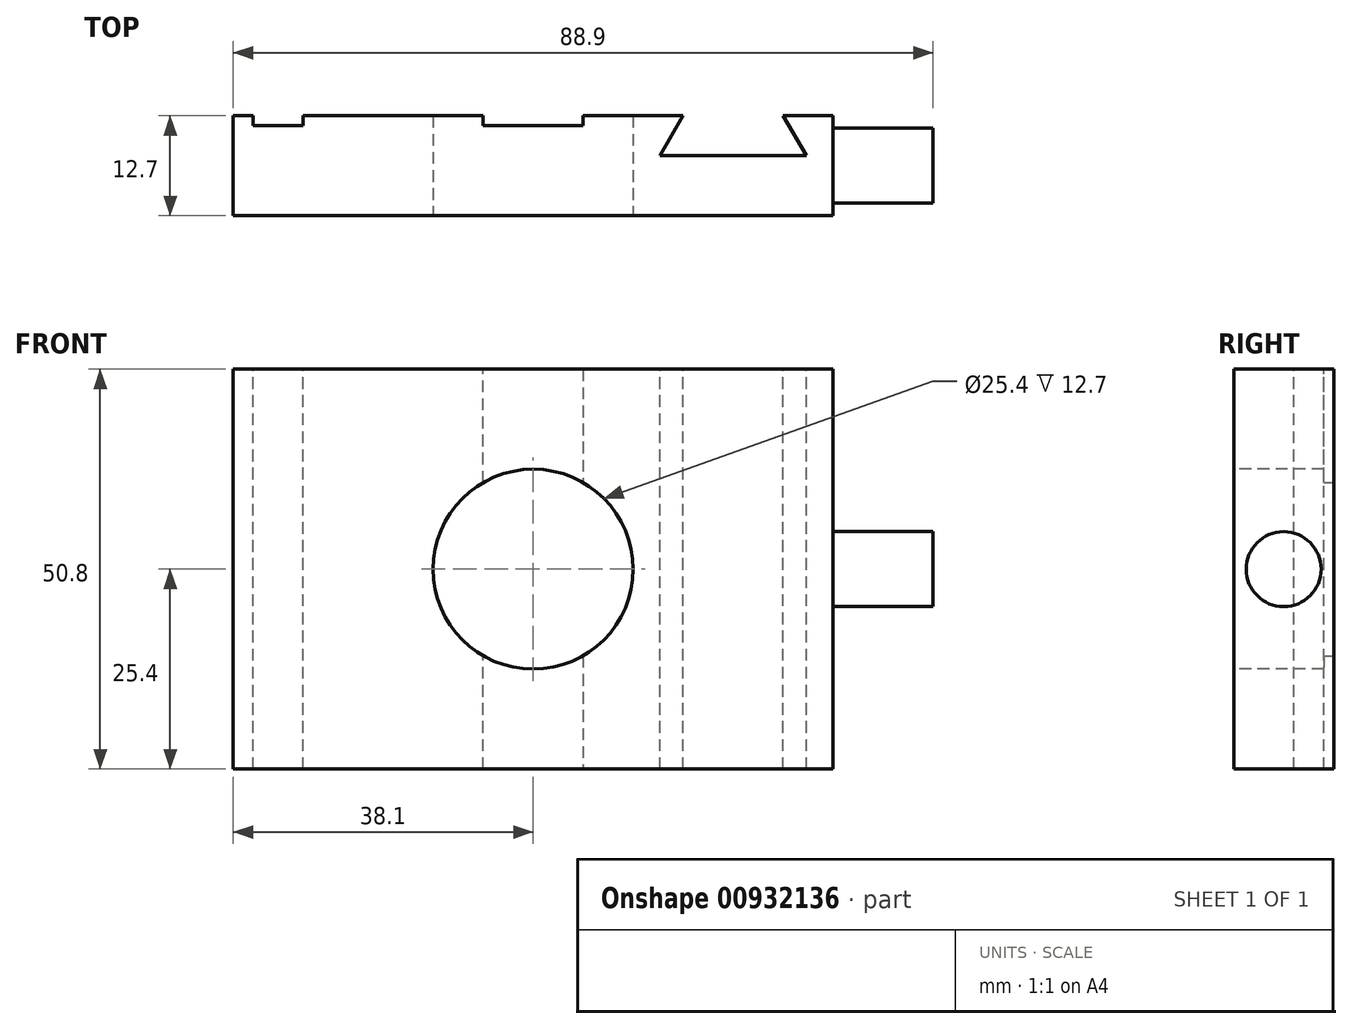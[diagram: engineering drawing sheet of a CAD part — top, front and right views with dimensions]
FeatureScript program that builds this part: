
annotation { "Feature Type Name" : "Feature", "Feature Type Description" : "" }
export const myFeature = defineFeature(function(context is Context, id is Id, definition is map)
    precondition{}
    {
        {
            var Q0;
            Q0=qCreatedBy(makeId("Front.planeOp"),FACE);
            var sketch = newSketch(context, id + "F0", { "sketchPlane" : qUnion([Q0])});
            skLineSegment(sketch, "E0.bottom", {"start": v(-38.1, 25.4) * mm, "end": v(38.1, 25.4) * mm});
            skLineSegment(sketch, "E0.top", {"start": v(-38.1, -25.4) * mm, "end": v(38.1, -25.4) * mm});
            skLineSegment(sketch, "E0.left", {"start": v(-38.1, 25.4) * mm, "end": v(-38.1, -25.4) * mm});
            skLineSegment(sketch, "E0.right", {"start": v(38.1, 25.4) * mm, "end": v(38.1, -25.4) * mm});
            skPoint(sketch, "E0.middle", {"position": v(0, 0) * mm});
            skCircle(sketch, "E1", {"center": v(0, 0) * mm, "radius": 12.7 * mm});
            skSolve(sketch);
        }
        {
            var Q0;
            Q0=makeQuery(id+"F0.imprint","IMPRINT",FACE,{"disambiguationData":[TD([[makeQuery(id+"F0.imprint","IMPRINT",EDGE,{"derivedFrom":sQuery(id+"F0.wireOp",EDGE,"E0.bottom")}),-1.0]])]});
            extrude(context, id + "F1", {"entities" : qUnion([Q0]), "oppositeDirection" : true, "depth" : 12.7 * mm, "offsetDistance" : 25.4 * mm});
        }
        {
            var Q0;
            Q0=makeQuery(id+"F1.opExtrude","CAP_FACE",FACE,{"disambiguationData":[OSD([sQuery(id+"F0.wireOp",EDGE,"E0.bottom"),sQuery(id+"F0.wireOp",EDGE,"E0.top"),sQuery(id+"F0.wireOp",EDGE,"E0.left"),sQuery(id+"F0.wireOp",EDGE,"E0.right"),sQuery(id+"F0.wireOp",EDGE,"E1")])],"isStart":false});
            var sketch = newSketch(context, id + "F2", { "sketchPlane" : qUnion([Q0])});
            skLineSegment(sketch, "E2.bottom", {"start": v(35.56, -25.4) * mm, "end": v(29.2, -25.4) * mm});
            skLineSegment(sketch, "E2.top", {"start": v(35.56, 25.4) * mm, "end": v(29.2, 25.4) * mm});
            skLineSegment(sketch, "E2.left", {"start": v(35.56, -25.4) * mm, "end": v(35.56, 25.4) * mm});
            skLineSegment(sketch, "E2.right", {"start": v(29.2, -25.4) * mm, "end": v(29.2, 25.4) * mm});
            skLineSegment(sketch, "E3", {"start": v(6.35, -25.4) * mm, "end": v(6.35, 25.4) * mm});
            skLineSegment(sketch, "E4", {"start": v(6.35, 25.4) * mm, "end": v(-6.35, 25.4) * mm});
            skLineSegment(sketch, "E5", {"start": v(-6.35, 25.4) * mm, "end": v(-6.35, -25.4) * mm});
            skPoint(sketch, "E6", {"position": v(0, 0) * mm});
            skPoint(sketch, "E7", {"position": v(0, 25.4) * mm});
            skLineSegment(sketch, "E8", {"start": v(0, 25.4) * mm, "end": v(0, -25.4) * mm, "construction": true});
            skSolve(sketch);
        }
        {
            var Q0;
            Q0=makeQuery(id+"F2.imprint","IMPRINT",FACE,{"disambiguationData":[TD([[makeQuery(id+"F2.imprint","IMPRINT",EDGE,{"derivedFrom":sQuery(id+"F2.wireOp",EDGE,"E2.bottom")}),-1.0]])]});
            var Q1;
            {var subQ0=sQuery(id+"F2.wireOp",EDGE,"E4");Q1=makeQuery(id+"F2.imprint","IMPRINT",FACE,{"disambiguationData":[TD([[makeQuery(id+"F2.imprint","IMPRINT",EDGE,{"derivedFrom":subQ0}),1.0]])]});}
            var Q2;
            {var subQ0=sQuery(id+"F2.wireOp",EDGE,"E3");var subQ1=makeQuery(id+"F1.opExtrude","CAP_EDGE",EDGE,{"disambiguationData":[OSD([sQuery(id+"F0.wireOp",EDGE,"E0.top")])],"isStart":false});var subQ2=makeQuery(id+"F2.imprint","INTERSECT",VERTEX,{"derivedFrom":[subQ1,subQ0]});Q2=makeQuery(id+"F2.imprint","IMPRINT",FACE,{"disambiguationData":[TD([[makeQuery(id+"F2.imprint","IMPRINT",EDGE,{"disambiguationData":[TD([[subQ2,-1.0]])],"derivedFrom":subQ0}),1.0]])]});}
            extrude(context, id + "F3", {"entities" : qUnion([Q0, Q1, Q2]), "operationType" : NewBodyOperationType.REMOVE, "oppositeDirection" : true, "depth" : 1.27 * mm, "offsetDistance" : 25.4 * mm});
        }
        {
            var Q0;
            Q0=makeQuery(id+"F1.opExtrude","SWEPT_FACE",FACE,{"disambiguationData":[OSD([sQuery(id+"F0.wireOp",EDGE,"E0.bottom")])]});
            var sketch = newSketch(context, id + "F4", { "sketchPlane" : qUnion([Q0])});
            skLineSegment(sketch, "E9", {"start": v(19.05, 12.7) * mm, "end": v(16.12, 7.62) * mm});
            skLineSegment(sketch, "E10", {"start": v(16.12, 7.62) * mm, "end": v(34.68, 7.62) * mm});
            skLineSegment(sketch, "E11", {"start": v(34.68, 7.62) * mm, "end": v(31.75, 12.7) * mm});
            skLineSegment(sketch, "E12", {"start": v(31.75, 12.7) * mm, "end": v(19.05, 12.7) * mm});
            skLineSegment(sketch, "E13", {"start": v(25.4, 7.62) * mm, "end": v(22.22, 12.7) * mm, "construction": true});
            skSolve(sketch);
        }
        {
            var Q0;
            Q0=makeQuery(id+"F4.imprint","IMPRINT",FACE,{"disambiguationData":[TD([[makeQuery(id+"F4.imprint","IMPRINT",EDGE,{"derivedFrom":sQuery(id+"F4.wireOp",EDGE,"E9")}),1.0]])]});
            extrude(context, id + "F5", {"entities" : qUnion([Q0]), "operationType" : NewBodyOperationType.REMOVE, "endBound" : BoundingType.THROUGH_ALL, "oppositeDirection" : true, "depth" : 25.4 * mm, "offsetDistance" : 25.4 * mm});
        }
        {
            var Q0;
            Q0=makeQuery(id+"F1.opExtrude","SWEPT_FACE",FACE,{"disambiguationData":[OSD([sQuery(id+"F0.wireOp",EDGE,"E0.right")])]});
            var sketch = newSketch(context, id + "F6", { "sketchPlane" : qUnion([Q0])});
            skCircle(sketch, "E14", {"center": v(6.35, 0) * mm, "radius": 4.76 * mm});
            skPoint(sketch, "E14.centerSnap0", {"position": v(12.7, 0) * mm});
            skPoint(sketch, "E14.centerSnap1", {"position": v(6.35, 25.4) * mm});
            skSolve(sketch);
        }
        {
            var Q0;
            Q0=makeQuery(id+"F6.imprint","IMPRINT",FACE,{"disambiguationData":[TD([[makeQuery(id+"F6.imprint","IMPRINT",EDGE,{"derivedFrom":sQuery(id+"F6.wireOp",EDGE,"E14")}),1.0]])]});
            extrude(context, id + "F7", {"entities" : qUnion([Q0]), "operationType" : NewBodyOperationType.ADD, "depth" : 12.7 * mm, "offsetDistance" : 25.4 * mm});
        }
    });
